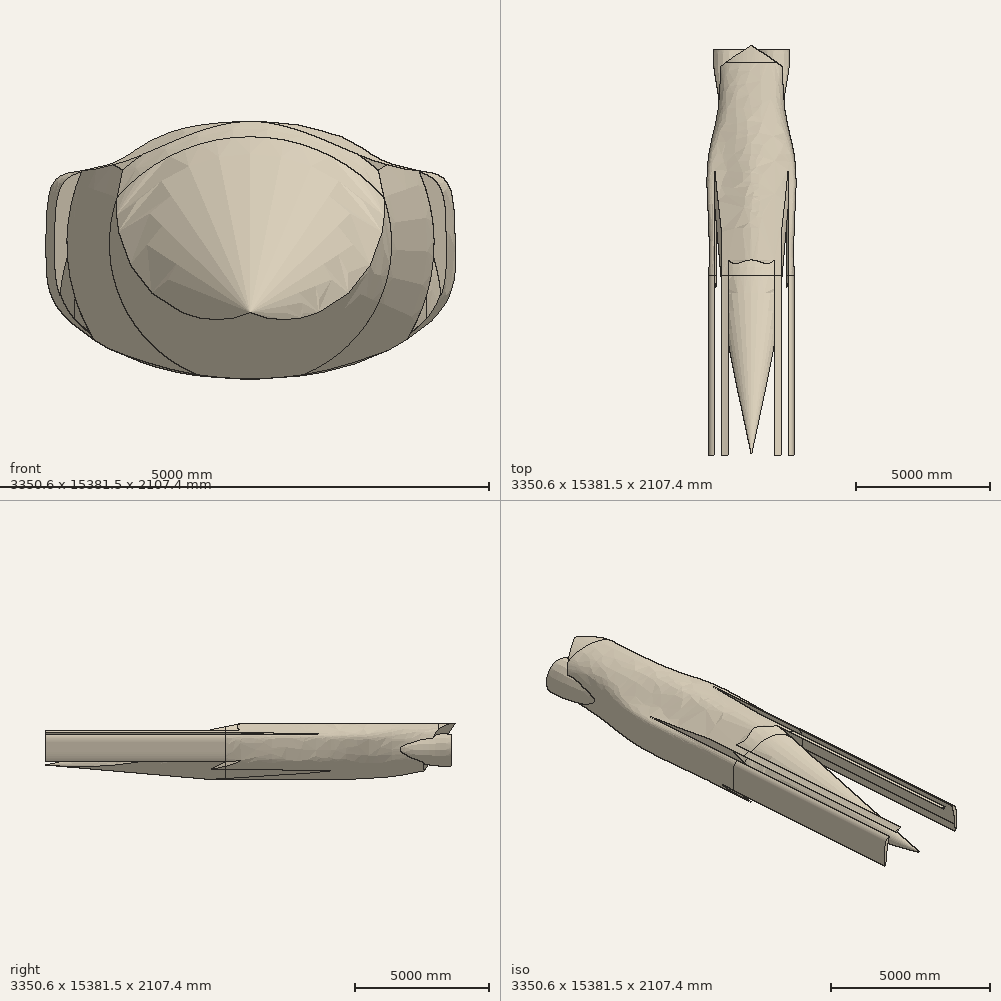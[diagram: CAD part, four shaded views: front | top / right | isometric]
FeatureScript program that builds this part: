
annotation { "Feature Type Name" : "Feature", "Feature Type Description" : "" }
export const myFeature = defineFeature(function(context is Context, id is Id, definition is map)
    precondition{}
    {
        {
            var Q0;
            Q0=qCreatedBy(makeId("Front.planeOp"),FACE);
            cPlane(context, id + "F0", {"entities" : qUnion([Q0]), "cplaneType" : CPlaneType.OFFSET, "offset" : 1750 * mm, "width" : 152.4 * mm, "height" : 152.4 * mm});
        }
        {
            var Q0;
            Q0=qCreatedBy(id+"F0.planeOp",FACE);
            var sketch = newSketch(context, id + "F1", { "sketchPlane" : qUnion([Q0])});
            skPoint(sketch, "E0.middle", {"position": v(0, 0) * mm});
            skFitSpline(sketch, "E1", {"points": [v(0, 1000) * mm, v(1060, 662.5) * mm, v(1517.6, 506.84) * mm, v(1600, 0) * mm, v(1517.6, -506.84) * mm, v(750, -1000) * mm, v(-750, -1000) * mm, v(-1517.6, -506.84) * mm, v(-1600, 0) * mm, v(-1517.6, 506.84) * mm, v(-1060, 662.5) * mm, v(0, 1000) * mm]});
            skSolve(sketch);
        }
        {
            var Q0;
            Q0=qCreatedBy(makeId("Front.planeOp"),FACE);
            var sketch = newSketch(context, id + "F2", { "sketchPlane" : qUnion([Q0])});
            skPoint(sketch, "E2.middle", {"position": v(0, 0) * mm});
            skFitSpline(sketch, "E3", {"points": [v(0, 1000) * mm, v(1060, 662.5) * mm, v(1517.6, 506.84) * mm, v(1600, 0) * mm, v(1517.6, -506.84) * mm, v(750, -1000) * mm, v(-750, -1000) * mm, v(-1517.6, -506.84) * mm, v(-1600, 0) * mm, v(-1517.6, 506.84) * mm, v(-1060, 662.5) * mm, v(0, 1000) * mm]});
            skSolve(sketch);
        }
        {
            var Q0;
            Q0=qCreatedBy(makeId("Front.planeOp"),FACE);
            cPlane(context, id + "F3", {"entities" : qUnion([Q0]), "cplaneType" : CPlaneType.OFFSET, "offset" : 2800 * mm, "oppositeDirection" : true, "width" : 150 * mm, "height" : 150 * mm});
        }
        {
            var Q0;
            Q0=qCreatedBy(id+"F3.planeOp",FACE);
            var sketch = newSketch(context, id + "F4", { "sketchPlane" : qUnion([Q0])});
            skPoint(sketch, "E4.middle", {"position": v(0, 0) * mm});
            skFitSpline(sketch, "E5", {"points": [v(0, 1000) * mm, v(1060, 662.5) * mm, v(1517.6, 506.84) * mm, v(1600, 0) * mm, v(1517.6, -506.84) * mm, v(750, -1000) * mm, v(-750, -1000) * mm, v(-1517.6, -506.84) * mm, v(-1600, 0) * mm, v(-1517.6, 506.84) * mm, v(-1060, 662.5) * mm, v(0, 1000) * mm]});
            skSolve(sketch);
        }
        {
            var Q0;
            Q0=qCreatedBy(makeId("Front.planeOp"),FACE);
            cPlane(context, id + "F5", {"entities" : qUnion([Q0]), "cplaneType" : CPlaneType.OFFSET, "offset" : 4500 * mm, "oppositeDirection" : true, "width" : 150 * mm, "height" : 150 * mm});
        }
        {
            var Q0;
            Q0=qCreatedBy(id+"F5.planeOp",FACE);
            var sketch = newSketch(context, id + "F6", { "sketchPlane" : qUnion([Q0])});
            skPoint(sketch, "E6.middle", {"position": v(0, 0) * mm});
            skFitSpline(sketch, "E7", {"points": [v(0, 1000) * mm, v(1060, 662.5) * mm, v(1250, 0) * mm, v(1060, -662.5) * mm, v(0, -1000) * mm, v(-1060, -662.5) * mm, v(-1250, 0) * mm, v(-1060, 662.5) * mm, v(0, 1000) * mm]});
            skSolve(sketch);
        }
        {
            var Q0;
            Q0=qCreatedBy(makeId("Front.planeOp"),FACE);
            cPlane(context, id + "F7", {"entities" : qUnion([Q0]), "cplaneType" : CPlaneType.OFFSET, "offset" : 6232.05 * mm, "oppositeDirection" : true, "width" : 150 * mm, "height" : 150 * mm});
        }
        {
            var Q0;
            Q0=qCreatedBy(id+"F7.planeOp",FACE);
            var sketch = newSketch(context, id + "F8", { "sketchPlane" : qUnion([Q0])});
            skPoint(sketch, "E8.middle", {"position": v(0, 0) * mm});
            skFitSpline(sketch, "E9", {"points": [v(0, 1000) * mm, v(1060, 662.5) * mm, v(1250, 0) * mm, v(848, -530) * mm, v(-848, -530) * mm, v(-1250, 0) * mm, v(-1060, 662.5) * mm, v(0, 1000) * mm]});
            skSolve(sketch);
        }
        {
            var Q0;
            Q0 = qSketchRegion(id + "F1", true);
            var Q1;
            Q1 = qSketchRegion(id + "F2", true);
            var Q2;
            Q2 = qSketchRegion(id + "F4", true);
            var Q3;
            Q3 = qSketchRegion(id + "F6", true);
            var Q4;
            Q4 = qSketchRegion(id + "F8", true);
            loft(context, id + "F9", {"sheetProfilesArray" : [{ "sheetProfileEntities" : qUnion([Q0]) }, { "sheetProfileEntities" : qUnion([Q1]) }, { "sheetProfileEntities" : qUnion([Q2]) }, { "sheetProfileEntities" : qUnion([Q3]) }, { "sheetProfileEntities" : qUnion([Q4]) }]});
        }
        {
            var Q0;
            Q0=makeQuery(id+"F9.opLoft","CAP_FACE",FACE,{"disambiguationData":[OSD([makeQuery(id+"F8.imprint","IMPRINT",FACE,{"disambiguationData":[TD([[makeQuery(id+"F8.imprint","IMPRINT",EDGE,{"derivedFrom":sQuery(id+"F8.wireOp",EDGE,"E9")}),-1.0]])]})])],"isStart":true});
            extrude(context, id + "F10", {"entities" : qUnion([Q0]), "operationType" : NewBodyOperationType.ADD, "depth" : 649.4 * mm});
        }
        {
            var Q0;
            Q0=qCreatedBy(makeId("Right.planeOp"),FACE);
            var sketch = newSketch(context, id + "F11", { "sketchPlane" : qUnion([Q0])});
            skLineSegment(sketch, "E10", {"start": v(0, 0) * mm, "end": v(4500, 0) * mm});
            skLineSegment(sketch, "E11", {"start": v(4500, 0) * mm, "end": v(6232.05, 0) * mm});
            skLineSegment(sketch, "E12", {"start": v(4500, 0) * mm, "end": v(4500, 1000) * mm});
            skLineSegment(sketch, "E13", {"start": v(4500, 1000) * mm, "end": v(6881.46, 1000) * mm});
            skLineSegment(sketch, "E14", {"start": v(6881.46, 1000) * mm, "end": v(6881.46, -1000) * mm});
            skLineSegment(sketch, "E15", {"start": v(6232.05, 0) * mm, "end": v(6881.46, 1000) * mm});
            skLineSegment(sketch, "E16", {"start": v(6232.05, 0) * mm, "end": v(5582.64, -1000) * mm});
            skLineSegment(sketch, "E17", {"start": v(5582.64, -1000) * mm, "end": v(6881.46, -1000) * mm});
            skSolve(sketch);
        }
        {
            var Q0;
            Q0=makeQuery(id+"F11.imprint","IMPRINT",FACE,{"disambiguationData":[TD([[makeQuery(id+"F11.imprint","IMPRINT",EDGE,{"derivedFrom":sQuery(id+"F11.wireOp",EDGE,"E14")}),-1.0]])]});
            var Q1;
            Q1=sQuery(id+"F11.wireOp",EDGE,"E13");
            revolve(context, id + "F12", {"operationType" : NewBodyOperationType.REMOVE, "entities" : qUnion([Q0]), "axis" : qUnion([Q1]), "revolveType" : RevolveType.SYMMETRIC, "oppositeDirection" : true, "angle" : 182 * degree});
        }
        {
            var Q0;
            Q0=makeQuery(id+"F9.opLoft","CAP_FACE",FACE,{"disambiguationData":[OSD([makeQuery(id+"F1.imprint","IMPRINT",FACE,{"disambiguationData":[TD([[makeQuery(id+"F1.imprint","IMPRINT",EDGE,{"derivedFrom":sQuery(id+"F1.wireOp",EDGE,"E1")}),-1.0]])]})])],"isStart":true});
            extrude(context, id + "F13", {"entities" : qUnion([Q0]), "depth" : 6750 * mm});
        }
        {
            var Q0;
            Q0=qCreatedBy(makeId("Right.planeOp"),FACE);
            var sketch = newSketch(context, id + "F14", { "sketchPlane" : qUnion([Q0])});
            skLineSegment(sketch, "E18", {"start": v(0, 0) * mm, "end": v(-3500, 0) * mm});
            skLineSegment(sketch, "E19", {"start": v(-3500, 0) * mm, "end": v(-3500, -1000) * mm});
            skLineSegment(sketch, "E20", {"start": v(-3500, -1000) * mm, "end": v(-8500, -1000) * mm});
            skLineSegment(sketch, "E21", {"start": v(-8500, -1000) * mm, "end": v(-8500, -562.56) * mm});
            skLineSegment(sketch, "E22", {"start": v(-1164.58, 0) * mm, "end": v(-1164.58, 1000) * mm});
            skLineSegment(sketch, "E23", {"start": v(-1164.58, 1000) * mm, "end": v(-8500, -562.56) * mm});
            skLineSegment(sketch, "E24", {"start": v(-8500, -562.56) * mm, "end": v(-3500, -1000) * mm});
            skLineSegment(sketch, "E25", {"start": v(-1164.58, 1000) * mm, "end": v(-8500, 1000) * mm});
            skLineSegment(sketch, "E26", {"start": v(-8500, 1000) * mm, "end": v(-8500, -562.56) * mm});
            skLineSegment(sketch, "E27", {"start": v(-8500, -1000) * mm, "end": v(-8500, -1500) * mm});
            skLineSegment(sketch, "E28", {"start": v(-3500, -1000) * mm, "end": v(2215.03, -1500) * mm});
            skLineSegment(sketch, "E29", {"start": v(2215.03, -1500) * mm, "end": v(-8500, -1500) * mm});
            skLineSegment(sketch, "E30", {"start": v(-8500, -562.56) * mm, "end": v(-3500, -562.56) * mm});
            skSolve(sketch);
        }
        {
            var Q0;
            Q0=makeQuery(id+"F14.imprint","IMPRINT",FACE,{"disambiguationData":[TD([[makeQuery(id+"F14.imprint","IMPRINT",EDGE,{"derivedFrom":sQuery(id+"F14.wireOp",EDGE,"E23")}),-1.0]])]});
            var Q1;
            Q1=sQuery(id+"F14.wireOp",EDGE,"E30");
            revolve(context, id + "F15", {"operationType" : NewBodyOperationType.REMOVE, "entities" : qUnion([Q0]), "axis" : qUnion([Q1]), "revolveType" : RevolveType.SYMMETRIC, "oppositeDirection" : true, "angle" : 250 * degree});
        }
        {
            var Q0;
            Q0=makeQuery(id+"F14.imprint","IMPRINT",FACE,{"disambiguationData":[TD([[makeQuery(id+"F14.imprint","IMPRINT",EDGE,{"derivedFrom":sQuery(id+"F14.wireOp",EDGE,"E20")}),-1.0]])]});
            var Q1;
            Q1=makeQuery(id+"F14.imprint","IMPRINT",FACE,{"disambiguationData":[TD([[makeQuery(id+"F14.imprint","IMPRINT",EDGE,{"derivedFrom":sQuery(id+"F14.wireOp",EDGE,"E20")}),1.0]])]});
            var Q2;
            Q2=sQuery(id+"F14.wireOp",EDGE,"E18");
            revolve(context, id + "F16", {"operationType" : NewBodyOperationType.REMOVE, "entities" : qUnion([Q0, Q1]), "axis" : qUnion([Q2]), "revolveType" : RevolveType.SYMMETRIC, "oppositeDirection" : true, "angle" : 240 * degree});
        }
        {
            var Q0;
            Q0=qCreatedBy(makeId("Front.planeOp"),FACE);
            cPlane(context, id + "F17", {"entities" : qUnion([Q0]), "cplaneType" : CPlaneType.OFFSET, "offset" : 3500 * mm, "oppositeDirection" : true, "width" : 150 * mm, "height" : 150 * mm});
        }
        {
            var Q0;
            Q0=qCreatedBy(id+"F17.planeOp",FACE);
            var sketch = newSketch(context, id + "F18", { "sketchPlane" : qUnion([Q0])});
            skCircle(sketch, "E31", {"center": v(-825, 0) * mm, "radius": 600 * mm});
            skCircle(sketch, "E32", {"center": v(825, 0) * mm, "radius": 600 * mm});
            skSolve(sketch);
        }
        {
            var Q0;
            Q0=qCreatedBy(makeId("Front.planeOp"),FACE);
            cPlane(context, id + "F19", {"entities" : qUnion([Q0]), "cplaneType" : CPlaneType.OFFSET, "offset" : 4500 * mm, "oppositeDirection" : true, "width" : 150 * mm, "height" : 150 * mm});
        }
        {
            var Q0;
            Q0=qCreatedBy(id+"F19.planeOp",FACE);
            var sketch = newSketch(context, id + "F20", { "sketchPlane" : qUnion([Q0])});
            skCircle(sketch, "E33", {"center": v(-825, 0) * mm, "radius": 400 * mm});
            skCircle(sketch, "E34", {"center": v(825, 0) * mm, "radius": 400 * mm});
            skSolve(sketch);
        }
        {
            var Q0;
            Q0=qCreatedBy(makeId("Front.planeOp"),FACE);
            cPlane(context, id + "F21", {"entities" : qUnion([Q0]), "cplaneType" : CPlaneType.OFFSET, "offset" : 6232.05 * mm, "oppositeDirection" : true, "width" : 150 * mm, "height" : 150 * mm});
        }
        {
            var Q0;
            Q0=qCreatedBy(id+"F21.planeOp",FACE);
            var sketch = newSketch(context, id + "F22", { "sketchPlane" : qUnion([Q0])});
            skCircle(sketch, "E35", {"center": v(-825, 0) * mm, "radius": 600 * mm});
            skCircle(sketch, "E36", {"center": v(825, 0) * mm, "radius": 600 * mm});
            skSolve(sketch);
        }
        {
            var Q0;
            Q0=qCreatedBy(makeId("Front.planeOp"),FACE);
            cPlane(context, id + "F23", {"entities" : qUnion([Q0]), "cplaneType" : CPlaneType.OFFSET, "offset" : 6732.05 * mm, "oppositeDirection" : true, "width" : 150 * mm, "height" : 150 * mm});
        }
        {
            var Q0;
            Q0=qCreatedBy(id+"F23.planeOp",FACE);
            var sketch = newSketch(context, id + "F24", { "sketchPlane" : qUnion([Q0])});
            skCircle(sketch, "E37", {"center": v(-825, 0) * mm, "radius": 600 * mm});
            skCircle(sketch, "E38", {"center": v(825, 0) * mm, "radius": 600 * mm});
            skSolve(sketch);
        }
        {
            var Q0;
            Q0=makeQuery(id+"F18.imprint","IMPRINT",FACE,{"disambiguationData":[TD([[makeQuery(id+"F18.imprint","IMPRINT",EDGE,{"derivedFrom":sQuery(id+"F18.wireOp",EDGE,"E31")}),1.0]])]});
            var Q1;
            Q1=makeQuery(id+"F20.imprint","IMPRINT",FACE,{"disambiguationData":[TD([[makeQuery(id+"F20.imprint","IMPRINT",EDGE,{"derivedFrom":sQuery(id+"F20.wireOp",EDGE,"E33")}),1.0]])]});
            var Q2;
            Q2=makeQuery(id+"F22.imprint","IMPRINT",FACE,{"disambiguationData":[TD([[makeQuery(id+"F22.imprint","IMPRINT",EDGE,{"derivedFrom":sQuery(id+"F22.wireOp",EDGE,"E35")}),1.0]])]});
            var Q3;
            Q3=makeQuery(id+"F24.imprint","IMPRINT",FACE,{"disambiguationData":[TD([[makeQuery(id+"F24.imprint","IMPRINT",EDGE,{"derivedFrom":sQuery(id+"F24.wireOp",EDGE,"E37")}),1.0]])]});
            loft(context, id + "F25", {"sheetProfilesArray" : [{ "sheetProfileEntities" : qUnion([Q0]) }, { "sheetProfileEntities" : qUnion([Q1]) }, { "sheetProfileEntities" : qUnion([Q2]) }, { "sheetProfileEntities" : qUnion([Q3]) }]});
        }
        {
            var Q0;
            Q0=makeQuery(id+"F18.imprint","IMPRINT",FACE,{"disambiguationData":[TD([[makeQuery(id+"F18.imprint","IMPRINT",EDGE,{"derivedFrom":sQuery(id+"F18.wireOp",EDGE,"E32")}),1.0]])]});
            var Q1;
            Q1=makeQuery(id+"F20.imprint","IMPRINT",FACE,{"disambiguationData":[TD([[makeQuery(id+"F20.imprint","IMPRINT",EDGE,{"derivedFrom":sQuery(id+"F20.wireOp",EDGE,"E34")}),1.0]])]});
            var Q2;
            Q2=makeQuery(id+"F22.imprint","IMPRINT",FACE,{"disambiguationData":[TD([[makeQuery(id+"F22.imprint","IMPRINT",EDGE,{"derivedFrom":sQuery(id+"F22.wireOp",EDGE,"E36")}),1.0]])]});
            var Q3;
            Q3=makeQuery(id+"F24.imprint","IMPRINT",FACE,{"disambiguationData":[TD([[makeQuery(id+"F24.imprint","IMPRINT",EDGE,{"derivedFrom":sQuery(id+"F24.wireOp",EDGE,"E38")}),1.0]])]});
            loft(context, id + "F26", {"sheetProfilesArray" : [{ "sheetProfileEntities" : qUnion([Q0]) }, { "sheetProfileEntities" : qUnion([Q1]) }, { "sheetProfileEntities" : qUnion([Q2]) }, { "sheetProfileEntities" : qUnion([Q3]) }]});
        }
    });
